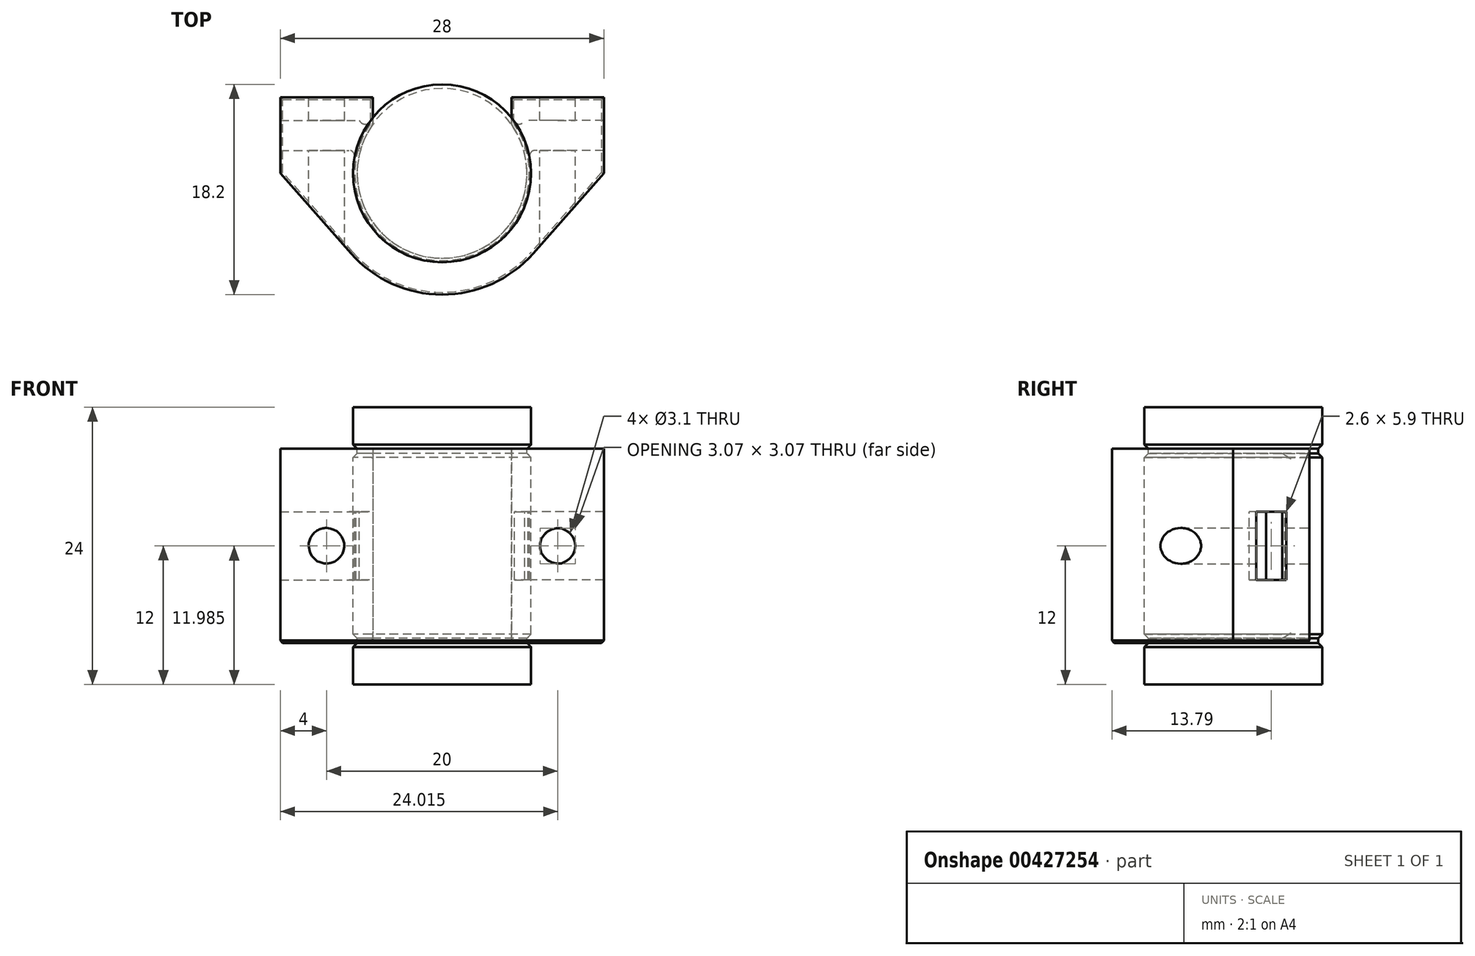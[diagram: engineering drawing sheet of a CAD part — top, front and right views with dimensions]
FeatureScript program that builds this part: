
annotation { "Feature Type Name" : "Feature", "Feature Type Description" : "" }
export const myFeature = defineFeature(function(context is Context, id is Id, definition is map)
    precondition{}
    {
        {
            var Q0;
            Q0=qCreatedBy(makeId("Front.planeOp"),FACE);
            var sketch = newSketch(context, id + "F0", { "sketchPlane" : qUnion([Q0])});
            skLineSegment(sketch, "E0", {"start": v(0, 12) * mm, "end": v(0, -12) * mm});
            skLineSegment(sketch, "E1.bottom", {"start": v(-4, 12) * mm, "end": v(-7.5, 12) * mm});
            skLineSegment(sketch, "E1.top", {"start": v(-4, -12) * mm, "end": v(-7.5, -12) * mm});
            skLineSegment(sketch, "E1.left", {"start": v(-4, 12) * mm, "end": v(-4, -12) * mm, "construction": true});
            skLineSegment(sketch, "E2", {"start": v(-7.5, 12) * mm, "end": v(-7.5, 8.75) * mm, "construction": true});
            skLineSegment(sketch, "E3", {"start": v(-7.5, 8.75) * mm, "end": v(-7.15, 8.75) * mm, "construction": true});
            skLineSegment(sketch, "E4", {"start": v(-7.15, 8.75) * mm, "end": v(-7.15, 7.65) * mm, "construction": true});
            skLineSegment(sketch, "E5", {"start": v(-7.15, 7.65) * mm, "end": v(-7.5, 7.65) * mm, "construction": true});
            skLineSegment(sketch, "E6", {"start": v(-7.5, 7.65) * mm, "end": v(-7.5, 0) * mm, "construction": true});
            skLineSegment(sketch, "E7.MirrorCS", {"start": v(-7.5, -8.75) * mm, "end": v(-7.15, -8.75) * mm, "construction": true});
            skLineSegment(sketch, "E8.MirrorCS", {"start": v(-7.15, -8.75) * mm, "end": v(-7.15, -7.65) * mm, "construction": true});
            skLineSegment(sketch, "E9.MirrorCS", {"start": v(-7.15, -7.65) * mm, "end": v(-7.5, -7.65) * mm, "construction": true});
            skLineSegment(sketch, "E10", {"start": v(-7.5, 0) * mm, "end": v(-7.5, -7.65) * mm, "construction": true});
            skLineSegment(sketch, "E11", {"start": v(-7.5, -8.75) * mm, "end": v(-7.5, -12) * mm, "construction": true});
            skLineSegment(sketch, "E12.0", {"start": v(-7.7, 12) * mm, "end": v(-7.7, 8.75) * mm});
            skLineSegment(sketch, "E13.0", {"start": v(-7.35, 8.75) * mm, "end": v(-7.35, 7.65) * mm});
            skLineSegment(sketch, "E14", {"start": v(-7.7, 8.75) * mm, "end": v(-7.35, 8.4) * mm});
            skLineSegment(sketch, "E15", {"start": v(-7.7, 7.65) * mm, "end": v(-7.7, 0) * mm});
            skLineSegment(sketch, "E16", {"start": v(-7.7, 7.65) * mm, "end": v(-7.35, 8) * mm});
            skLineSegment(sketch, "E17", {"start": v(-7.7, 12) * mm, "end": v(-7.5, 12) * mm});
            skLineSegment(sketch, "E18.MirrorCS", {"start": v(-7.7, -7.65) * mm, "end": v(-7.7, 0) * mm});
            skLineSegment(sketch, "E19.MirrorCS", {"start": v(-7.7, -7.65) * mm, "end": v(-7.35, -8) * mm});
            skLineSegment(sketch, "E20.MirrorCS", {"start": v(-7.35, -8.75) * mm, "end": v(-7.35, -7.65) * mm});
            skLineSegment(sketch, "E21.MirrorCS", {"start": v(-7.7, -8.75) * mm, "end": v(-7.35, -8.4) * mm});
            skLineSegment(sketch, "E22.MirrorCS", {"start": v(-7.7, -12) * mm, "end": v(-7.7, -8.75) * mm});
            skLineSegment(sketch, "E23.MirrorCS", {"start": v(-7.7, -12) * mm, "end": v(-7.5, -12) * mm});
            skLineSegment(sketch, "E24", {"start": v(-4, 12) * mm, "end": v(0, 12) * mm});
            skLineSegment(sketch, "E25", {"start": v(-4, -12) * mm, "end": v(0, -12) * mm});
            skSolve(sketch);
        }
        {
            var Q0;
            Q0=qCreatedBy(makeId("Top.planeOp"),FACE);
            var sketch = newSketch(context, id + "F1", { "sketchPlane" : qUnion([Q0])});
            skLineSegment(sketch, "E26", {"start": v(-5, 6.6) * mm, "end": v(5, 6.6) * mm, "construction": true});
            skCircle(sketch, "E27", {"center": v(0, 0) * mm, "radius": 7.5 * mm, "construction": true});
            skLineSegment(sketch, "E28", {"start": v(5, 6.6) * mm, "end": v(5, 5.6) * mm, "construction": true});
            skLineSegment(sketch, "E29", {"start": v(-5, 6.6) * mm, "end": v(-5, 5.6) * mm, "construction": true});
            skLineSegment(sketch, "E30", {"start": v(-5, 6.6) * mm, "end": v(-10, 6.6) * mm, "construction": true});
            skLineSegment(sketch, "E31", {"start": v(5, 6.6) * mm, "end": v(10, 6.6) * mm, "construction": true});
            skLineSegment(sketch, "E32", {"start": v(-10, 6.6) * mm, "end": v(-10, 4.6) * mm, "construction": true});
            skLineSegment(sketch, "E33.bottom", {"start": v(-12.85, 4.6) * mm, "end": v(-7.15, 4.6) * mm, "construction": true});
            skLineSegment(sketch, "E33.top", {"start": v(-12.85, 2) * mm, "end": v(-7.15, 2) * mm, "construction": true});
            skLineSegment(sketch, "E33.left", {"start": v(-12.85, 4.6) * mm, "end": v(-12.85, 2) * mm, "construction": true});
            skLineSegment(sketch, "E33.right", {"start": v(-7.15, 4.6) * mm, "end": v(-7.15, 2) * mm, "construction": true});
            skSolve(sketch);
        }
        {
            var Q0;
            Q0=qSketchRegion(id+"F0",true);
            var Q1;
            Q1=sQuery(id+"F0.wireOp",EDGE,"E0");
            revolve(context, id + "F2", {"entities" : qUnion([Q0]), "axis" : qUnion([Q1]), "revolveType" : RevolveType.FULL});
        }
        {
            var Q0;
            Q0=qCreatedBy(makeId("Top.planeOp"),FACE);
            var sketch = newSketch(context, id + "F3", { "sketchPlane" : qUnion([Q0])});
            skPoint(sketch, "E34.0", {"position": v(0, 6.6) * mm});
            skLineSegment(sketch, "E35", {"start": v(0, 6.6) * mm, "end": v(-14, 6.6) * mm, "construction": true});
            skLineSegment(sketch, "E36", {"start": v(-14, 6.6) * mm, "end": v(-14, 0) * mm});
            skLineSegment(sketch, "E37.MirrorCS", {"start": v(0, 6.6) * mm, "end": v(14, 6.6) * mm, "construction": true});
            skLineSegment(sketch, "E38.MirrorCS", {"start": v(14, 6.6) * mm, "end": v(14, 0) * mm});
            skCircle(sketch, "E39.0", {"center": v(0, 0) * mm, "radius": 7.5 * mm, "construction": true});
            skCircle(sketch, "E40.0", {"center": v(0, 0) * mm, "radius": 10.5 * mm, "construction": true});
            skArc(sketch, "E41", {"start": v(-7.88, -6.95) * mm, "mid": v(0, -10.5) * mm, "end": v(7.88, -6.95) * mm});
            skLineSegment(sketch, "E42", {"start": v(-14, 0) * mm, "end": v(-7.87, -6.95) * mm});
            skLineSegment(sketch, "E43.MirrorCS", {"start": v(14, 0) * mm, "end": v(7.87, -6.95) * mm});
            skLineSegment(sketch, "E44.0", {"start": v(-12.85, 4.6) * mm, "end": v(-7.15, 4.6) * mm, "construction": true});
            skLineSegment(sketch, "E45.0", {"start": v(-12.85, 2) * mm, "end": v(-7.15, 2) * mm, "construction": true});
            skLineSegment(sketch, "E46.0", {"start": v(-12.85, 4.6) * mm, "end": v(-12.85, 2) * mm, "construction": true});
            skLineSegment(sketch, "E47", {"start": v(-14, 6.6) * mm, "end": v(-6, 6.6) * mm});
            skLineSegment(sketch, "E48.MirrorCS", {"start": v(14, 6.6) * mm, "end": v(6, 6.6) * mm});
            skLineSegment(sketch, "E49.0", {"start": v(-7.15, 4.6) * mm, "end": v(-7.15, 2) * mm, "construction": true});
            skLineSegment(sketch, "E50", {"start": v(-6, 6.6) * mm, "end": v(-6, 3.3) * mm});
            skPoint(sketch, "E50.endSnap0", {"position": v(-7.15, 3.3) * mm});
            skLineSegment(sketch, "E51", {"start": v(-6, 3.3) * mm, "end": v(0, 3.3) * mm});
            skLineSegment(sketch, "E52.MirrorCS", {"start": v(6, 6.6) * mm, "end": v(6, 3.3) * mm});
            skLineSegment(sketch, "E53.MirrorCS", {"start": v(6, 3.3) * mm, "end": v(0, 3.3) * mm});
            skSolve(sketch);
        }
        {
            var Q0;
            Q0=qSketchRegion(id+"F3",true);
            var Q1;
            Q1=sQuery(id+"F0.wireOp",VERTEX,"E14.end");
            var Q2;
            Q2=sQuery(id+"F0.wireOp",VERTEX,"E21.MirrorCS.end");
            extrude(context, id + "F4", {"entities" : qUnion([Q0]), "endBound" : BoundingType.UP_TO_VERTEX, "endBoundEntityVertex" : qUnion([Q1]), "depth" : 25 * mm, "hasSecondDirection" : true, "secondDirectionBound" : SecondDirectionBoundingType.UP_TO_VERTEX, "secondDirectionOppositeDirection" : true, "secondDirectionBoundEntityVertex" : qUnion([Q2]), "secondDirectionDepth" : 25 * mm});
        }
        {
            var Q0;
            Q0=makeQuery(id+"F4.opExtrude","SWEPT_FACE",FACE,{"disambiguationData":[OSD([sQuery(id+"F3.wireOp",EDGE,"E48.MirrorCS")])]});
            var sketch = newSketch(context, id + "F5", { "sketchPlane" : qUnion([Q0])});
            skPoint(sketch, "E54.0", {"position": v(-10, 0) * mm});
            skPoint(sketch, "E55.0", {"position": v(10, 0) * mm});
            skSolve(sketch);
        }
        {
            var Q0;
            Q0=makeQuery(id+"F2.opRevolve","SWEPT_BODY",BODY,{"disambiguationData":[OSD([sQuery(id+"F0.wireOp",EDGE,"E0"),sQuery(id+"F0.wireOp",EDGE,"E1.bottom"),sQuery(id+"F0.wireOp",EDGE,"E1.top"),sQuery(id+"F0.wireOp",EDGE,"E12.0"),sQuery(id+"F0.wireOp",EDGE,"E13.0"),sQuery(id+"F0.wireOp",EDGE,"E14"),sQuery(id+"F0.wireOp",EDGE,"E15"),sQuery(id+"F0.wireOp",EDGE,"E16"),sQuery(id+"F0.wireOp",EDGE,"E17"),sQuery(id+"F0.wireOp",EDGE,"E18.MirrorCS"),sQuery(id+"F0.wireOp",EDGE,"E19.MirrorCS"),sQuery(id+"F0.wireOp",EDGE,"E20.MirrorCS"),sQuery(id+"F0.wireOp",EDGE,"E21.MirrorCS"),sQuery(id+"F0.wireOp",EDGE,"E22.MirrorCS"),sQuery(id+"F0.wireOp",EDGE,"E23.MirrorCS"),sQuery(id+"F0.wireOp",EDGE,"E24"),sQuery(id+"F0.wireOp",EDGE,"E25")])]});
            var Q1;
            Q1=makeQuery(id+"F4.opExtrude","SWEPT_BODY",BODY,{"disambiguationData":[OSD([sQuery(id+"F3.wireOp",EDGE,"E36"),sQuery(id+"F3.wireOp",EDGE,"E38.MirrorCS"),sQuery(id+"F3.wireOp",EDGE,"E41"),sQuery(id+"F3.wireOp",EDGE,"E42"),sQuery(id+"F3.wireOp",EDGE,"E43.MirrorCS"),sQuery(id+"F3.wireOp",EDGE,"E47"),sQuery(id+"F3.wireOp",EDGE,"E48.MirrorCS"),sQuery(id+"F3.wireOp",EDGE,"E50"),sQuery(id+"F3.wireOp",EDGE,"E51"),sQuery(id+"F3.wireOp",EDGE,"E52.MirrorCS"),sQuery(id+"F3.wireOp",EDGE,"E53.MirrorCS")])]});
            booleanBodies(context, id + "F6", {"operationType" : BooleanOperationType.SUBTRACTION, "tools" : qUnion([Q0]), "targets" : qUnion([Q1]), "keepTools" : true});
        }
        {
            var Q0;
            Q0=sQuery(id+"F5.wireOp",VERTEX,"E54.0");
            var Q1;
            Q1=sQuery(id+"F5.wireOp",VERTEX,"E55.0");
            var Q2;
            Q2=makeQuery(id+"F4.opExtrude","SWEPT_BODY",BODY,{"disambiguationData":[OSD([sQuery(id+"F3.wireOp",EDGE,"E36"),sQuery(id+"F3.wireOp",EDGE,"E38.MirrorCS"),sQuery(id+"F3.wireOp",EDGE,"E41"),sQuery(id+"F3.wireOp",EDGE,"E42"),sQuery(id+"F3.wireOp",EDGE,"E43.MirrorCS"),sQuery(id+"F3.wireOp",EDGE,"E47"),sQuery(id+"F3.wireOp",EDGE,"E48.MirrorCS"),sQuery(id+"F3.wireOp",EDGE,"E50"),sQuery(id+"F3.wireOp",EDGE,"E51"),sQuery(id+"F3.wireOp",EDGE,"E52.MirrorCS"),sQuery(id+"F3.wireOp",EDGE,"E53.MirrorCS")])]});
            hole(context, id + "F7", {"style" : HoleStyle.SIMPLE, "endStyle" : HoleEndStyle.THROUGH, "holeDiameter" : 3.1 * mm, "isTappedThrough" : true, "tappedDepth" : 12 * mm, "tapClearance" : 3, "locations" : qUnion([Q0, Q1]), "scope" : qUnion([Q2])});
        }
        {
            var Q0;
            Q0=qCreatedBy(makeId("Top.planeOp"),FACE);
            var sketch = newSketch(context, id + "F8", { "sketchPlane" : qUnion([Q0])});
            skLineSegment(sketch, "E56.0", {"start": v(-12.85, 2) * mm, "end": v(-7.15, 2) * mm});
            skLineSegment(sketch, "E57.0", {"start": v(-12.85, 4.6) * mm, "end": v(-12.85, 2) * mm, "construction": true});
            skLineSegment(sketch, "E58.0", {"start": v(-12.85, 4.6) * mm, "end": v(-7.15, 4.6) * mm});
            skLineSegment(sketch, "E59.0", {"start": v(-7.15, 4.6) * mm, "end": v(-7.15, 2) * mm});
            skLineSegment(sketch, "E60.MirrorCS", {"start": v(12.85, 4.6) * mm, "end": v(7.15, 4.6) * mm});
            skLineSegment(sketch, "E61.MirrorCS", {"start": v(12.85, 4.6) * mm, "end": v(12.85, 2) * mm, "construction": true});
            skLineSegment(sketch, "E62.MirrorCS", {"start": v(12.85, 2) * mm, "end": v(7.15, 2) * mm});
            skLineSegment(sketch, "E63.MirrorCS", {"start": v(7.15, 4.6) * mm, "end": v(7.15, 2) * mm});
            skLineSegment(sketch, "E64", {"start": v(-12.85, 4.6) * mm, "end": v(-19.02, 4.6) * mm});
            skLineSegment(sketch, "E65", {"start": v(-19.02, 4.6) * mm, "end": v(-19.02, 2) * mm});
            skLineSegment(sketch, "E66", {"start": v(-19.02, 2) * mm, "end": v(-12.85, 2) * mm});
            skLineSegment(sketch, "E67.MirrorCS", {"start": v(12.85, 4.6) * mm, "end": v(19.02, 4.6) * mm});
            skLineSegment(sketch, "E68.MirrorCS", {"start": v(19.02, 4.6) * mm, "end": v(19.02, 2) * mm});
            skLineSegment(sketch, "E69.MirrorCS", {"start": v(19.02, 2) * mm, "end": v(12.85, 2) * mm});
            skSolve(sketch);
        }
        {
            var Q0;
            Q0=qSketchRegion(id+"F8",true);
            extrude(context, id + "F9", {"entities" : qUnion([Q0]), "operationType" : NewBodyOperationType.REMOVE, "endBound" : BoundingType.SYMMETRIC, "depth" : (0.4 + 5.5) * mm});
        }
        {
            var Q0;
            Q0=makeQuery(id+"F4.opExtrude","TWEAK_EDGE",EDGE,{"derivedFrom":[makeQuery(id+"F3.imprint","IMPRINT",EDGE,{"derivedFrom":sQuery(id+"F3.wireOp",EDGE,"E47")}),makeQuery(id+"F3.imprint","IMPRINT",EDGE,{"derivedFrom":sQuery(id+"F3.wireOp",EDGE,"E50")})]});
            var Q1;
            Q1=makeQuery(id+"F4.opExtrude","TWEAK_EDGE",EDGE,{"derivedFrom":[makeQuery(id+"F3.imprint","IMPRINT",EDGE,{"derivedFrom":sQuery(id+"F3.wireOp",EDGE,"E36")}),makeQuery(id+"F3.imprint","IMPRINT",EDGE,{"derivedFrom":sQuery(id+"F3.wireOp",EDGE,"E47")})]});
            var Q2;
            Q2=makeQuery(id+"F4.opExtrude","TWEAK_EDGE",EDGE,{"derivedFrom":[makeQuery(id+"F3.imprint","IMPRINT",EDGE,{"derivedFrom":sQuery(id+"F3.wireOp",EDGE,"E48.MirrorCS")}),makeQuery(id+"F3.imprint","IMPRINT",EDGE,{"derivedFrom":sQuery(id+"F3.wireOp",EDGE,"E52.MirrorCS")})]});
            var Q3;
            Q3=makeQuery(id+"F4.opExtrude","TWEAK_EDGE",EDGE,{"derivedFrom":[makeQuery(id+"F3.imprint","IMPRINT",EDGE,{"derivedFrom":sQuery(id+"F3.wireOp",EDGE,"E38.MirrorCS")}),makeQuery(id+"F3.imprint","IMPRINT",EDGE,{"derivedFrom":sQuery(id+"F3.wireOp",EDGE,"E48.MirrorCS")})]});
            var Q4;
            Q4=makeQuery(id+"F6.opBoolean","INTERSECT",EDGE,{"derivedFrom":[makeQuery(id+"F2.opRevolve","SWEPT_FACE",FACE,{"disambiguationData":[OSD([sQuery(id+"F0.wireOp",EDGE,"E15"),sQuery(id+"F0.wireOp",EDGE,"E18.MirrorCS")])]}),makeQuery(id+"F4.opExtrude","SWEPT_FACE",FACE,{"disambiguationData":[OSD([sQuery(id+"F3.wireOp",EDGE,"E52.MirrorCS")])]})]});
            var Q5;
            Q5=makeQuery(id+"F6.opBoolean","INTERSECT",EDGE,{"derivedFrom":[makeQuery(id+"F2.opRevolve","SWEPT_FACE",FACE,{"disambiguationData":[OSD([sQuery(id+"F0.wireOp",EDGE,"E15"),sQuery(id+"F0.wireOp",EDGE,"E18.MirrorCS")])]}),makeQuery(id+"F4.opExtrude","SWEPT_FACE",FACE,{"disambiguationData":[OSD([sQuery(id+"F3.wireOp",EDGE,"E50")])]})]});
            var Q6;
            Q6=makeQuery(id+"F6.opBoolean","INTERSECT",EDGE,{"derivedFrom":[makeQuery(id+"F2.opRevolve","SWEPT_FACE",FACE,{"disambiguationData":[OSD([sQuery(id+"F0.wireOp",EDGE,"E13.0")])]}),makeQuery(id+"F4.opExtrude","SWEPT_FACE",FACE,{"disambiguationData":[OSD([sQuery(id+"F3.wireOp",EDGE,"E50")])]})]});
            var Q7;
            Q7=makeQuery(id+"F6.opBoolean","INTERSECT",EDGE,{"derivedFrom":[makeQuery(id+"F2.opRevolve","SWEPT_FACE",FACE,{"disambiguationData":[OSD([sQuery(id+"F0.wireOp",EDGE,"E20.MirrorCS")])]}),makeQuery(id+"F4.opExtrude","SWEPT_FACE",FACE,{"disambiguationData":[OSD([sQuery(id+"F3.wireOp",EDGE,"E50")])]})]});
            var Q8;
            Q8=makeQuery(id+"F6.opBoolean","INTERSECT",EDGE,{"derivedFrom":[makeQuery(id+"F2.opRevolve","SWEPT_FACE",FACE,{"disambiguationData":[OSD([sQuery(id+"F0.wireOp",EDGE,"E13.0")])]}),makeQuery(id+"F4.opExtrude","SWEPT_FACE",FACE,{"disambiguationData":[OSD([sQuery(id+"F3.wireOp",EDGE,"E52.MirrorCS")])]})]});
            var Q9;
            Q9=makeQuery(id+"F6.opBoolean","INTERSECT",EDGE,{"derivedFrom":[makeQuery(id+"F2.opRevolve","SWEPT_FACE",FACE,{"disambiguationData":[OSD([sQuery(id+"F0.wireOp",EDGE,"E20.MirrorCS")])]}),makeQuery(id+"F4.opExtrude","SWEPT_FACE",FACE,{"disambiguationData":[OSD([sQuery(id+"F3.wireOp",EDGE,"E52.MirrorCS")])]})]});
            var Q10;
            Q10=makeQuery(id+"F4.opExtrude","TWEAK_EDGE",EDGE,{"derivedFrom":[makeQuery(id+"F3.imprint","IMPRINT",EDGE,{"derivedFrom":sQuery(id+"F3.wireOp",EDGE,"E36")}),makeQuery(id+"F3.imprint","IMPRINT",EDGE,{"derivedFrom":sQuery(id+"F3.wireOp",EDGE,"E42")})]});
            var Q11;
            Q11=makeQuery(id+"F4.opExtrude","TWEAK_EDGE",EDGE,{"derivedFrom":[makeQuery(id+"F3.imprint","IMPRINT",EDGE,{"derivedFrom":sQuery(id+"F3.wireOp",EDGE,"E38.MirrorCS")}),makeQuery(id+"F3.imprint","IMPRINT",EDGE,{"derivedFrom":sQuery(id+"F3.wireOp",EDGE,"E43.MirrorCS")})]});
            var Q12;
            Q12=makeQuery(id+"F9.boolean.opBoolean","INTERSECT",EDGE,{"derivedFrom":[makeQuery(id+"F6.opBoolean","COPY",FACE,{"derivedFrom":makeQuery(id+"F2.opRevolve","SWEPT_FACE",FACE,{"disambiguationData":[OSD([sQuery(id+"F0.wireOp",EDGE,"E15"),sQuery(id+"F0.wireOp",EDGE,"E18.MirrorCS")])]})}),makeQuery(id+"F9.opExtrude","SWEPT_FACE",FACE,{"disambiguationData":[OSD([sQuery(id+"F8.wireOp",EDGE,"E59.0")])]})]});
            var Q13;
            Q13=makeQuery(id+"F9.boolean.opBoolean","INTERSECT",EDGE,{"derivedFrom":[makeQuery(id+"F6.opBoolean","COPY",FACE,{"derivedFrom":makeQuery(id+"F2.opRevolve","SWEPT_FACE",FACE,{"disambiguationData":[OSD([sQuery(id+"F0.wireOp",EDGE,"E15"),sQuery(id+"F0.wireOp",EDGE,"E18.MirrorCS")])]})}),makeQuery(id+"F9.opExtrude","SWEPT_FACE",FACE,{"disambiguationData":[OSD([sQuery(id+"F8.wireOp",EDGE,"E63.MirrorCS")])]})]});
            var Q14;
            Q14=makeQuery(id+"F9.boolean.opBoolean","INTERSECT",EDGE,{"derivedFrom":[makeQuery(id+"F6.opBoolean","COPY",FACE,{"derivedFrom":makeQuery(id+"F2.opRevolve","SWEPT_FACE",FACE,{"disambiguationData":[OSD([sQuery(id+"F0.wireOp",EDGE,"E15"),sQuery(id+"F0.wireOp",EDGE,"E18.MirrorCS")])]})}),makeQuery(id+"F9.opExtrude","SWEPT_FACE",FACE,{"disambiguationData":[OSD([sQuery(id+"F8.wireOp",EDGE,"E56.0"),sQuery(id+"F8.wireOp",EDGE,"E66")])]})]});
            var Q15;
            Q15=makeQuery(id+"F9.boolean.opBoolean","INTERSECT",EDGE,{"derivedFrom":[makeQuery(id+"F6.opBoolean","COPY",FACE,{"derivedFrom":makeQuery(id+"F2.opRevolve","SWEPT_FACE",FACE,{"disambiguationData":[OSD([sQuery(id+"F0.wireOp",EDGE,"E15"),sQuery(id+"F0.wireOp",EDGE,"E18.MirrorCS")])]})}),makeQuery(id+"F9.opExtrude","SWEPT_FACE",FACE,{"disambiguationData":[OSD([sQuery(id+"F8.wireOp",EDGE,"E62.MirrorCS"),sQuery(id+"F8.wireOp",EDGE,"E69.MirrorCS")])]})]});
            fillet(context, id + "F10", {"entities" : qUnion([Q0, Q1, Q2, Q3, Q4, Q5, Q6, Q7, Q8, Q9, Q10, Q11, Q12, Q13, Q14, Q15]), "radius" : .5 * mm, "allowEdgeOverflow" : false});
        }
        {
            var Q0;
            Q0=makeQuery(id+"F4.opExtrude","CAP_FACE",FACE,{"disambiguationData":[OSD([sQuery(id+"F3.wireOp",EDGE,"E36"),sQuery(id+"F3.wireOp",EDGE,"E38.MirrorCS"),sQuery(id+"F3.wireOp",EDGE,"E41"),sQuery(id+"F3.wireOp",EDGE,"E42"),sQuery(id+"F3.wireOp",EDGE,"E43.MirrorCS"),sQuery(id+"F3.wireOp",EDGE,"E47"),sQuery(id+"F3.wireOp",EDGE,"E48.MirrorCS"),sQuery(id+"F3.wireOp",EDGE,"E50"),sQuery(id+"F3.wireOp",EDGE,"E51"),sQuery(id+"F3.wireOp",EDGE,"E52.MirrorCS"),sQuery(id+"F3.wireOp",EDGE,"E53.MirrorCS")])],"isStart":true});
            chamfer(context, id + "F11", {"entities" : qUnion([Q0]), "width" : .2 * mm});
        }
    });
